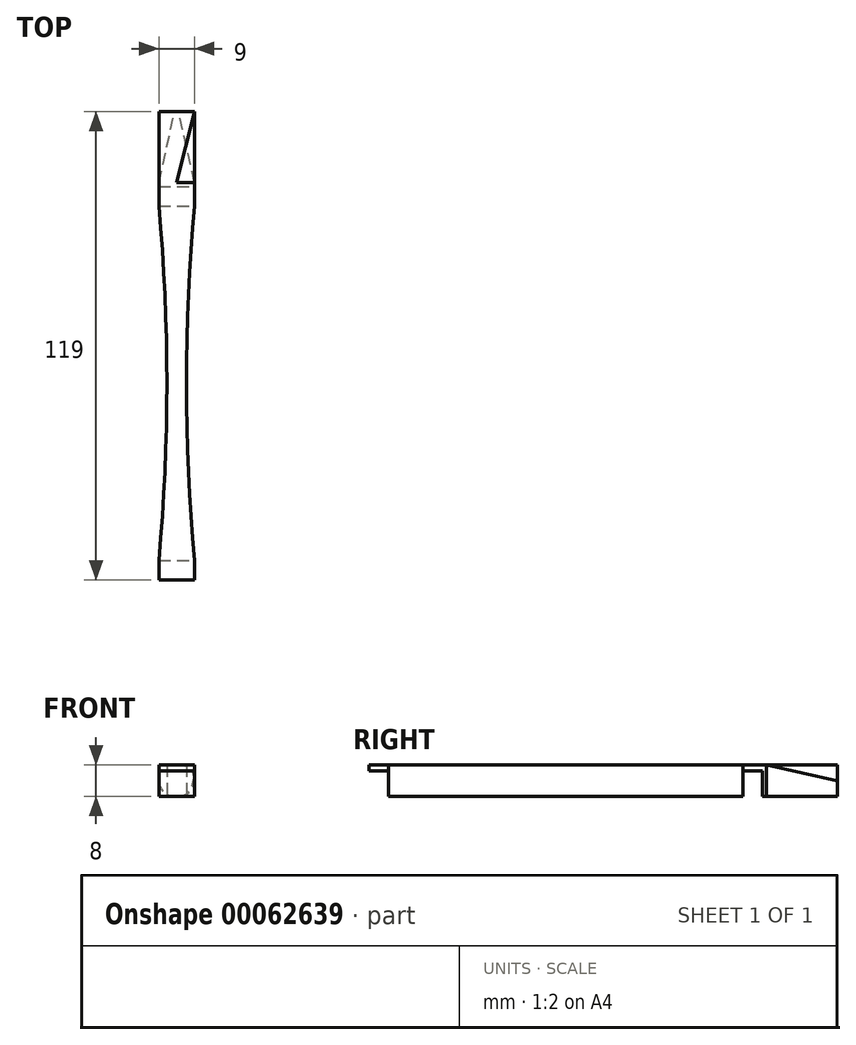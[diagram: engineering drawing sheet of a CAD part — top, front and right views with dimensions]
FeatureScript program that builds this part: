
annotation { "Feature Type Name" : "Feature", "Feature Type Description" : "" }
export const myFeature = defineFeature(function(context is Context, id is Id, definition is map)
    precondition{}
    {
        {
            var Q0;
            Q0=qCreatedBy(makeId("Front.planeOp"),FACE);
            var sketch = newSketch(context, id + "F0", { "sketchPlane" : qUnion([Q0])});
            skLineSegment(sketch, "E0.rect.bottom", {"start": v(4.5, -4) * mm, "end": v(-4.5, -4) * mm});
            skLineSegment(sketch, "E0.rect.top", {"start": v(4.5, 4) * mm, "end": v(-4.5, 4) * mm});
            skLineSegment(sketch, "E0.rect.left", {"start": v(4.5, -4) * mm, "end": v(4.5, 4) * mm});
            skLineSegment(sketch, "E0.rect.right", {"start": v(-4.5, -4) * mm, "end": v(-4.5, 4) * mm});
            skPoint(sketch, "E0.rect.middle", {"position": v(0, 0) * mm});
            skSolve(sketch);
        }
        {
            var Q0;
            Q0 = qSketchRegion(id + "F0", true);
            extrude(context, id + "F1", {"entities" : qUnion([Q0]), "depth" : 101 * mm, "symmetric" : true});
        }
        {
            var Q0;
            Q0=qCreatedBy(makeId("Right.planeOp"),FACE);
            var sketch = newSketch(context, id + "F2", { "sketchPlane" : qUnion([Q0])});
            skLineSegment(sketch, "E1.0", {"start": v(-50.5, -4) * mm, "end": v(-50.5, 4) * mm});
            skLineSegment(sketch, "E2.bottom", {"start": v(-50.5, -4) * mm, "end": v(-45.5, -4) * mm});
            skLineSegment(sketch, "E2.top", {"start": v(-50.5, 2.5) * mm, "end": v(-45.5, 2.5) * mm});
            skLineSegment(sketch, "E2.left", {"start": v(-50.5, -4) * mm, "end": v(-50.5, 2.5) * mm});
            skLineSegment(sketch, "E2.right", {"start": v(-45.5, -4) * mm, "end": v(-45.5, 2.5) * mm});
            skLineSegment(sketch, "E3", {"start": v(-45.5, 0) * mm, "end": v(44.5, 0) * mm, "construction": true});
            skPoint(sketch, "E3.startSnap0", {"position": v(-45.5, -0.75) * mm});
            skLineSegment(sketch, "E4.0", {"start": v(-50.5, -4) * mm, "end": v(50.5, -4) * mm});
            skLineSegment(sketch, "E5.bottom", {"start": v(44.5, 2.5) * mm, "end": v(49.5, 2.5) * mm});
            skLineSegment(sketch, "E5.top", {"start": v(44.5, -4) * mm, "end": v(49.5, -4) * mm});
            skLineSegment(sketch, "E5.left", {"start": v(44.5, 2.5) * mm, "end": v(44.5, -4) * mm});
            skLineSegment(sketch, "E5.right", {"start": v(49.5, 2.5) * mm, "end": v(49.5, -4) * mm});
            skSolve(sketch);
        }
        {
            var Q0;
            Q0 = qSketchRegion(id + "F2", true);
            var Q1;
            Q1=makeQuery(id+"F1.opExtrude","SWEPT_FACE",FACE,{"disambiguationData":[OSD([sQuery(id+"F0.wireOp",EDGE,"E0.rect.left")])]});
            var Q2;
            Q2=makeQuery(id+"F1.opExtrude","SWEPT_FACE",FACE,{"disambiguationData":[OSD([sQuery(id+"F0.wireOp",EDGE,"E0.rect.right")])]});
            extrude(context, id + "F3", {"entities" : qUnion([Q0]), "operationType" : NewBodyOperationType.REMOVE, "endBound" : BoundingType.THROUGH_ALL, "oppositeDirection" : true, "endBoundEntityFace" : qUnion([Q1]), "depth" : 25 * mm, "hasSecondDirection" : true, "secondDirectionBound" : BoundingType.THROUGH_ALL, "secondDirectionOppositeDirection" : false, "secondDirectionBoundEntityFace" : qUnion([Q2]), "secondDirectionDepth" : 25 * mm});
        }
        {
            var Q0;
            Q0=makeQuery(id+"F1.opExtrude","CAP_FACE",FACE,{"disambiguationData":[OSD([sQuery(id+"F0.wireOp",EDGE,"E0.rect.bottom"),sQuery(id+"F0.wireOp",EDGE,"E0.rect.top"),sQuery(id+"F0.wireOp",EDGE,"E0.rect.left"),sQuery(id+"F0.wireOp",EDGE,"E0.rect.right")])],"isStart":true});
            cPlane(context, id + "F4", {"entities" : qUnion([Q0]), "cplaneType" : CPlaneType.OFFSET, "offset" : 18 * mm, "width" : 150 * mm, "height" : 150 * mm});
        }
        {
            var Q0;
            Q0=qCreatedBy(id+"F4.planeOp",FACE);
            var sketch = newSketch(context, id + "F5", { "sketchPlane" : qUnion([Q0])});
            skLineSegment(sketch, "E6.0.0", {"start": v(-0.5, -4) * mm, "end": v(0.5, -4) * mm});
            skLineSegment(sketch, "E6.0.1", {"start": v(4.5, 0) * mm, "end": v(4.5, 4) * mm});
            skLineSegment(sketch, "E6.0.2", {"start": v(4.5, 4) * mm, "end": v(-4.5, 4) * mm});
            skLineSegment(sketch, "E6.0.3", {"start": v(-4.5, 4) * mm, "end": v(-4.5, 0) * mm});
            skPoint(sketch, "E7.visualSharp", {"position": v(4.5, -4) * mm});
            skArc(sketch, "E7.filletArc", {"start": v(0.5, -4) * mm, "mid": v(3.33, -2.83) * mm, "end": v(4.5, 0) * mm});
            skPoint(sketch, "E8.visualSharp", {"position": v(-4.5, -4) * mm});
            skArc(sketch, "E8.filletArc", {"start": v(-4.5, 0) * mm, "mid": v(-3.33, -2.83) * mm, "end": v(-0.5, -4) * mm});
            skSolve(sketch);
        }
        {
            var Q1;
            Q1=makeQuery(id+"F1.opExtrude","CAP_FACE",FACE,{"disambiguationData":[OSD([sQuery(id+"F0.wireOp",EDGE,"E0.rect.bottom"),sQuery(id+"F0.wireOp",EDGE,"E0.rect.top"),sQuery(id+"F0.wireOp",EDGE,"E0.rect.left"),sQuery(id+"F0.wireOp",EDGE,"E0.rect.right")])],"isStart":true});
            var Q2;
            Q2=makeQuery(id+"F5.imprint","IMPRINT",FACE,{"disambiguationData":[TD([[makeQuery(id+"F5.imprint","IMPRINT",EDGE,{"derivedFrom":sQuery(id+"F5.wireOp",EDGE,"E6.0.0")}),1.0]])]});
            loft(context, id + "F6", {"operationType" : NewBodyOperationType.ADD, "sheetProfilesArray" : [{ "sheetProfileEntities" : qUnion([Q1]) }, { "sheetProfileEntities" : qUnion([Q2]) }]});
        }
        {
            var Q0;
            Q0=makeQuery(id+"F3.boolean.opBoolean","SPLIT",FACE,{"disambiguationData":[TD([makeQuery(id+"F3.opExtrude","SWEPT_FACE",FACE,{"disambiguationData":[OSD([sQuery(id+"F2.wireOp",EDGE,"E2.right")])]})])],"derivedFrom":makeQuery(id+"F1.opExtrude","SWEPT_FACE",FACE,{"disambiguationData":[OSD([sQuery(id+"F0.wireOp",EDGE,"E0.rect.bottom")])]})});
            var sketch = newSketch(context, id + "F7", { "sketchPlane" : qUnion([Q0])});
            skArc(sketch, "E9", {"start": v(-4.5, -44.5) * mm, "mid": v(-2.5, 0.5) * mm, "end": v(-4.5, 45.5) * mm});
            skArc(sketch, "E10", {"start": v(4.5, 45.5) * mm, "mid": v(2.5, 0.5) * mm, "end": v(4.5, -44.5) * mm});
            skLineSegment(sketch, "E11", {"start": v(-4.5, 45.5) * mm, "end": v(-4.5, -44.5) * mm});
            skLineSegment(sketch, "E12", {"start": v(4.5, 45.5) * mm, "end": v(4.5, -44.5) * mm});
            skSolve(sketch);
        }
        {
            var Q0;
            Q0 = qSketchRegion(id + "F7", true);
            extrude(context, id + "F8", {"entities" : qUnion([Q0]), "operationType" : NewBodyOperationType.REMOVE, "endBound" : BoundingType.THROUGH_ALL, "oppositeDirection" : true, "depth" : 25 * mm});
        }
    });
